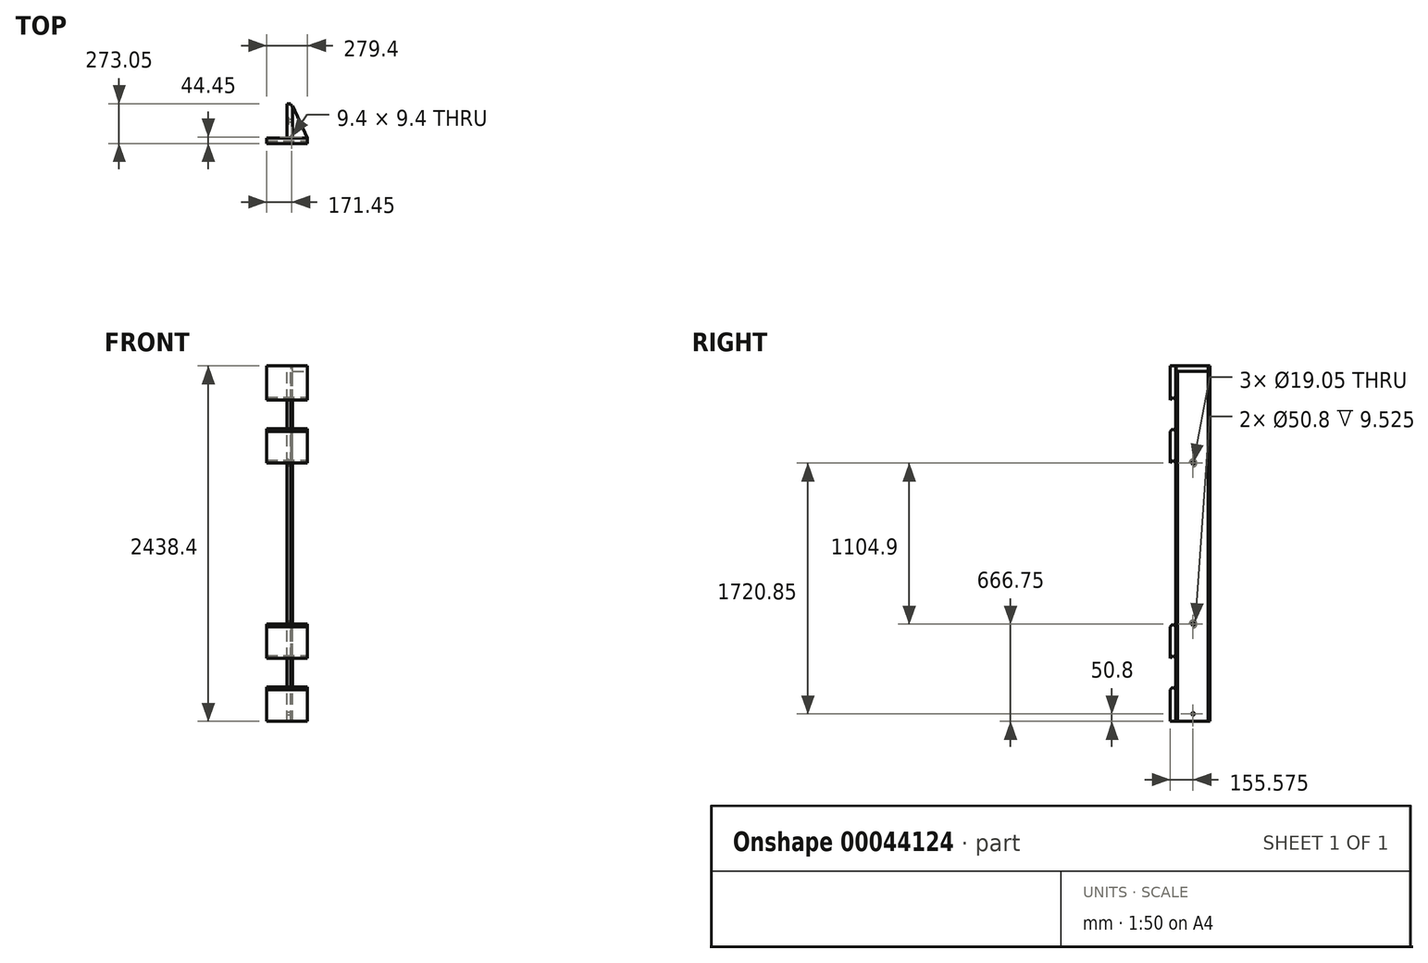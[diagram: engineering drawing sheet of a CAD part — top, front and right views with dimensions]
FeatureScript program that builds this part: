
annotation { "Feature Type Name" : "Feature", "Feature Type Description" : "" }
export const myFeature = defineFeature(function(context is Context, id is Id, definition is map)
    precondition{}
    {
        {
            var Q0;
            Q0=qCreatedBy(makeId("Right.planeOp"),FACE);
            var sketch = newSketch(context, id + "F0", { "sketchPlane" : qUnion([Q0])});
            skLineSegment(sketch, "E0.bottom", {"start": v(0, 0) * mm, "end": v(234.95, 0) * mm});
            skLineSegment(sketch, "E0.top", {"start": v(0, 2438.4) * mm, "end": v(234.95, 2438.4) * mm});
            skLineSegment(sketch, "E0.left", {"start": v(0, 0) * mm, "end": v(0, 2438.4) * mm});
            skLineSegment(sketch, "E0.right", {"start": v(234.95, 0) * mm, "end": v(234.95, 2438.4) * mm});
            skCircle(sketch, "E1", {"center": v(117.47, 1771.65) * mm, "radius": 9.53 * mm});
            skPoint(sketch, "E1.centerSnap0", {"position": v(117.47, 2438.4) * mm});
            skCircle(sketch, "E2", {"center": v(117.47, 666.75) * mm, "radius": 9.53 * mm});
            skPoint(sketch, "E2.centerSnap0", {"position": v(117.48, 0) * mm});
            skCircle(sketch, "E3", {"center": v(117.48, 50.8) * mm, "radius": 9.53 * mm});
            skSolve(sketch);
        }
        {
            var Q0;
            Q0 = qSketchRegion(id + "F0", true);
            extrude(context, id + "F1", {"entities" : qUnion([Q0]), "depth" : 38.1 * mm});
        }
        {
            var Q0;
            Q0=makeQuery(id+"F1.opExtrude","CAP_FACE",FACE,{"disambiguationData":[OSD([sQuery(id+"F0.wireOp",EDGE,"E0.bottom"),sQuery(id+"F0.wireOp",EDGE,"E0.top"),sQuery(id+"F0.wireOp",EDGE,"E0.left"),sQuery(id+"F0.wireOp",EDGE,"E0.right")])],"isStart":false});
            var sketch = newSketch(context, id + "F2", { "sketchPlane" : qUnion([Q0])});
            skLineSegment(sketch, "E4", {"start": v(0, 0) * mm, "end": v(0, 234.95) * mm, "construction": true});
            skLineSegment(sketch, "E5", {"start": v(0, 234.95) * mm, "end": v(-38.1, 234.95) * mm, "construction": true});
            skLineSegment(sketch, "E6", {"start": v(-38.1, 234.95) * mm, "end": v(-38.1, 0) * mm, "construction": true});
            skLineSegment(sketch, "E7", {"start": v(-38.1, 0) * mm, "end": v(0, 0) * mm});
            skLineSegment(sketch, "E8", {"start": v(-19.05, 234.95) * mm, "end": v(-38.1, 215.9) * mm});
            skLineSegment(sketch, "E9", {"start": v(-38.1, 215.9) * mm, "end": v(-38.1, 0) * mm});
            skPoint(sketch, "E10.endSnap0", {"position": v(-19.05, 0) * mm});
            skLineSegment(sketch, "E11", {"start": v(0, 215.9) * mm, "end": v(0, 0) * mm});
            skLineSegment(sketch, "E12", {"start": v(0, 215.9) * mm, "end": v(-19.05, 234.95) * mm});
            skLineSegment(sketch, "E13", {"start": v(0, 431.8) * mm, "end": v(-19.05, 450.85) * mm});
            skLineSegment(sketch, "E14", {"start": v(-19.05, 450.85) * mm, "end": v(-38.1, 431.8) * mm});
            skLineSegment(sketch, "E15", {"start": v(-38.1, 431.8) * mm, "end": v(-38.1, 647.7) * mm});
            skLineSegment(sketch, "E16", {"start": v(-38.1, 647.7) * mm, "end": v(-19.05, 666.75) * mm});
            skLineSegment(sketch, "E17", {"start": v(-19.05, 666.75) * mm, "end": v(0, 647.7) * mm});
            skLineSegment(sketch, "E18", {"start": v(0, 647.7) * mm, "end": v(0, 431.8) * mm});
            skLineSegment(sketch, "E19", {"start": v(0, 2438.4) * mm, "end": v(-38.1, 2438.4) * mm});
            skLineSegment(sketch, "E20", {"start": v(-38.1, 2438.4) * mm, "end": v(-38.1, 2203.45) * mm});
            skLineSegment(sketch, "E21", {"start": v(-38.1, 2203.45) * mm, "end": v(-19.05, 2222.5) * mm});
            skPoint(sketch, "E21.endSnap0", {"position": v(-19.05, 2438.4) * mm});
            skLineSegment(sketch, "E22", {"start": v(-19.05, 2222.5) * mm, "end": v(0, 2203.45) * mm});
            skLineSegment(sketch, "E23", {"start": v(0, 2203.45) * mm, "end": v(0, 2438.4) * mm});
            skLineSegment(sketch, "E24", {"start": v(0, 1987.55) * mm, "end": v(-19.05, 2006.6) * mm});
            skLineSegment(sketch, "E25", {"start": v(-19.05, 2006.6) * mm, "end": v(-38.1, 1987.55) * mm});
            skLineSegment(sketch, "E26", {"start": v(-38.1, 1987.55) * mm, "end": v(-38.1, 1771.65) * mm});
            skLineSegment(sketch, "E27", {"start": v(-38.1, 1771.65) * mm, "end": v(-19.05, 1790.7) * mm});
            skLineSegment(sketch, "E28", {"start": v(-19.05, 1790.7) * mm, "end": v(0, 1771.65) * mm});
            skLineSegment(sketch, "E29", {"start": v(0, 1771.65) * mm, "end": v(0, 1987.55) * mm});
            skSolve(sketch);
        }
        {
            var Q0;
            Q0 = qSketchRegion(id + "F2", true);
            extrude(context, id + "F3", {"entities" : qUnion([Q0]), "oppositeDirection" : true, "depth" : 177.8 * mm, "hasSecondDirection" : true, "secondDirectionOppositeDirection" : false, "secondDirectionDepth" : 101.6 * mm});
        }
        {
            var Q0;
            Q0=makeQuery(id+"F1.opExtrude","SWEPT_FACE",FACE,{"disambiguationData":[OSD([sQuery(id+"F0.wireOp",EDGE,"E0.top")])]});
            var sketch = newSketch(context, id + "F4", { "sketchPlane" : qUnion([Q0])});
            skLineSegment(sketch, "E30.bottom", {"start": v(38.1, 234.95) * mm, "end": v(25.4, 234.95) * mm});
            skLineSegment(sketch, "E30.top", {"start": v(38.1, 222.25) * mm, "end": v(25.4, 222.25) * mm});
            skLineSegment(sketch, "E30.left", {"start": v(38.1, 234.95) * mm, "end": v(38.1, 222.25) * mm});
            skLineSegment(sketch, "E30.right", {"start": v(25.4, 234.95) * mm, "end": v(25.4, 222.25) * mm});
            skLineSegment(sketch, "E31.bottom", {"start": v(38.1, 0) * mm, "end": v(25.4, 0) * mm});
            skLineSegment(sketch, "E31.top", {"start": v(38.1, 12.7) * mm, "end": v(25.4, 12.7) * mm});
            skLineSegment(sketch, "E31.left", {"start": v(38.1, 0) * mm, "end": v(38.1, 12.7) * mm});
            skLineSegment(sketch, "E31.right", {"start": v(25.4, 0) * mm, "end": v(25.4, 12.7) * mm});
            skSolve(sketch);
        }
        {
            var Q0;
            Q0 = qSketchRegion(id + "F4", true);
            extrude(context, id + "F5", {"entities" : qUnion([Q0]), "operationType" : NewBodyOperationType.REMOVE, "endBound" : BoundingType.THROUGH_ALL, "oppositeDirection" : true, "depth" : 25.4 * mm});
        }
        {
            var Q0;
            Q0=makeQuery(id+"F1.opExtrude","SWEPT_FACE",FACE,{"disambiguationData":[OSD([sQuery(id+"F0.wireOp",EDGE,"E0.top")])]});
            var sketch = newSketch(context, id + "F6", { "sketchPlane" : qUnion([Q0])});
            skLineSegment(sketch, "E32", {"start": v(38.1, 222.25) * mm, "end": v(38.1, 0) * mm});
            skLineSegment(sketch, "E33", {"start": v(38.1, 0) * mm, "end": v(139.7, 0) * mm});
            skLineSegment(sketch, "E34", {"start": v(139.7, 0) * mm, "end": v(38.1, 222.25) * mm});
            skSolve(sketch);
        }
        {
            var Q0;
            Q0 = qSketchRegion(id + "F6", true);
            extrude(context, id + "F7", {"entities" : qUnion([Q0]), "oppositeDirection" : true, "depth" : 38.1 * mm});
        }
        {
            var Q0;
            Q0=makeQuery(id+"F1.opExtrude","SWEPT_FACE",FACE,{"disambiguationData":[OSD([sQuery(id+"F0.wireOp",EDGE,"E0.top")])]});
            var sketch = newSketch(context, id + "F8", { "sketchPlane" : qUnion([Q0])});
            skLineSegment(sketch, "E35.bottom", {"start": v(25.4, 0) * mm, "end": v(38.1, 0) * mm});
            skLineSegment(sketch, "E35.top", {"start": v(25.4, 12.7) * mm, "end": v(38.1, 12.7) * mm});
            skLineSegment(sketch, "E35.left", {"start": v(25.4, 0) * mm, "end": v(25.4, 12.7) * mm});
            skLineSegment(sketch, "E35.right", {"start": v(38.1, 0) * mm, "end": v(38.1, 12.7) * mm});
            skLineSegment(sketch, "E36.bottom", {"start": v(27.05, 1.65) * mm, "end": v(36.45, 1.65) * mm});
            skLineSegment(sketch, "E36.top", {"start": v(27.05, 11.05) * mm, "end": v(36.45, 11.05) * mm});
            skLineSegment(sketch, "E36.left", {"start": v(27.05, 1.65) * mm, "end": v(27.05, 11.05) * mm});
            skLineSegment(sketch, "E36.right", {"start": v(36.45, 1.65) * mm, "end": v(36.45, 11.05) * mm});
            skSolve(sketch);
        }
        {
            var Q0;
            Q0 = qSketchRegion(id + "F8", true);
            extrude(context, id + "F9", {"entities" : qUnion([Q0]), "oppositeDirection" : true, "depth" : 2438.4 * mm});
        }
        {
            var Q0;
            Q0=makeQuery(id+"F1.opExtrude","CAP_FACE",FACE,{"disambiguationData":[OSD([sQuery(id+"F0.wireOp",EDGE,"E0.bottom"),sQuery(id+"F0.wireOp",EDGE,"E0.top"),sQuery(id+"F0.wireOp",EDGE,"E0.left"),sQuery(id+"F0.wireOp",EDGE,"E0.right"),sQuery(id+"F0.wireOp",EDGE,"E1"),sQuery(id+"F0.wireOp",EDGE,"E2")])],"isStart":true});
            var sketch = newSketch(context, id + "F10", { "sketchPlane" : qUnion([Q0])});
            skCircle(sketch, "E37", {"center": v(-117.47, 1771.65) * mm, "radius": 25.4 * mm});
            skCircle(sketch, "E38", {"center": v(-117.47, 666.75) * mm, "radius": 25.4 * mm});
            skSolve(sketch);
        }
        {
            var Q0;
            Q0 = qSketchRegion(id + "F10", true);
            extrude(context, id + "F11", {"entities" : qUnion([Q0]), "operationType" : NewBodyOperationType.REMOVE, "oppositeDirection" : true, "depth" : 9.52 * mm});
        }
    });
